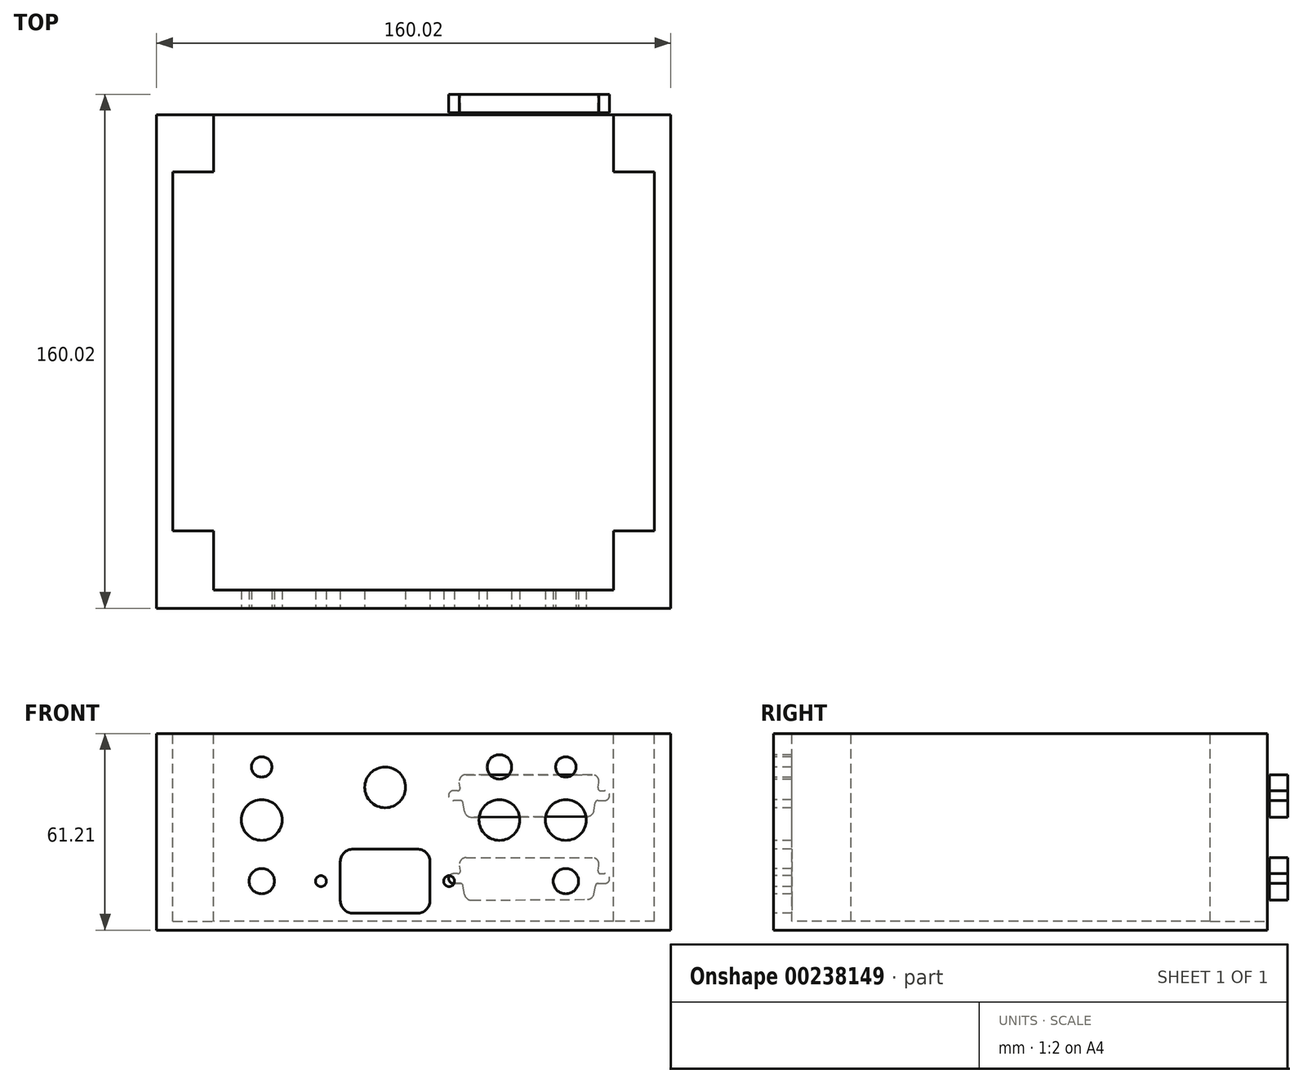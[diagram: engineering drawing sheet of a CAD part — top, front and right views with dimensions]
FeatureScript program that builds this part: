
annotation { "Feature Type Name" : "Feature", "Feature Type Description" : "" }
export const myFeature = defineFeature(function(context is Context, id is Id, definition is map)
    precondition{}
    {
        {
            var Q0;
            Q0=qCreatedBy(makeId("Top.planeOp"),FACE);
            var sketch = newSketch(context, id + "F0", { "sketchPlane" : qUnion([Q0])});
            skLineSegment(sketch, "E0.bottom", {"start": v(0, 0) * mm, "end": v(160.02, 0) * mm});
            skLineSegment(sketch, "E0.top", {"start": v(0, 160.02) * mm, "end": v(160.02, 160.02) * mm});
            skLineSegment(sketch, "E0.left", {"start": v(0, 0) * mm, "end": v(0, 160.02) * mm});
            skLineSegment(sketch, "E0.right", {"start": v(160.02, 0) * mm, "end": v(160.02, 160.02) * mm});
            skSolve(sketch);
        }
        {
            var Q0;
            Q0=makeQuery(id+"F0.imprint","IMPRINT",FACE,{"disambiguationData":[TD([[makeQuery(id+"F0.imprint","IMPRINT",EDGE,{"derivedFrom":sQuery(id+"F0.wireOp",EDGE,"E0.bottom")}),1.0]])]});
            extrude(context, id + "F1", {"entities" : qUnion([Q0]), "oppositeDirection" : true, "depth" : 61.2 * mm});
        }
        {
            var Q0;
            Q0=makeQuery(id+"F1.opExtrude","CAP_FACE",FACE,{"disambiguationData":[OSD([sQuery(id+"F0.wireOp",EDGE,"E0.bottom"),sQuery(id+"F0.wireOp",EDGE,"E0.top"),sQuery(id+"F0.wireOp",EDGE,"E0.left"),sQuery(id+"F0.wireOp",EDGE,"E0.right")])],"isStart":true});
            var sketch = newSketch(context, id + "F2", { "sketchPlane" : qUnion([Q0])});
            skLineSegment(sketch, "E1.bottom", {"start": v(5.08, 154.3) * mm, "end": v(154.94, 154.3) * mm});
            skLineSegment(sketch, "E1.top", {"start": v(5.08, 5.71) * mm, "end": v(154.94, 5.72) * mm});
            skLineSegment(sketch, "E1.left", {"start": v(5.08, 154.3) * mm, "end": v(5.08, 5.71) * mm});
            skLineSegment(sketch, "E1.right", {"start": v(154.94, 154.3) * mm, "end": v(154.94, 5.72) * mm});
            skLineSegment(sketch, "E2", {"start": v(5.08, 24.13) * mm, "end": v(17.78, 24.13) * mm});
            skLineSegment(sketch, "E3", {"start": v(17.78, 24.13) * mm, "end": v(17.78, 5.71) * mm});
            skLineSegment(sketch, "E4", {"start": v(154.94, 24.13) * mm, "end": v(142.24, 24.13) * mm});
            skLineSegment(sketch, "E5", {"start": v(142.24, 24.13) * mm, "end": v(142.24, 5.72) * mm});
            skLineSegment(sketch, "E6", {"start": v(5.08, 135.9) * mm, "end": v(17.78, 135.9) * mm});
            skLineSegment(sketch, "E7", {"start": v(17.78, 135.9) * mm, "end": v(17.78, 154.3) * mm});
            skLineSegment(sketch, "E8", {"start": v(154.94, 135.9) * mm, "end": v(142.24, 135.9) * mm});
            skLineSegment(sketch, "E9", {"start": v(142.24, 135.9) * mm, "end": v(142.24, 154.3) * mm});
            skSolve(sketch);
        }
        {
            var Q0;
            {var subQ3=sQuery(id+"F2.wireOp",EDGE,"E2");Q0=makeQuery(id+"F2.imprint","IMPRINT",FACE,{"disambiguationData":[TD([[makeQuery(id+"F2.imprint","IMPRINT",EDGE,{"derivedFrom":subQ3}),1.0]])]});}
            extrude(context, id + "F3", {"entities" : qUnion([Q0]), "operationType" : NewBodyOperationType.REMOVE, "oppositeDirection" : true, "depth" : 58.42 * mm});
        }
        {
            var Q0;
            Q0=makeQuery(id+"F1.opExtrude","SWEPT_FACE",FACE,{"disambiguationData":[OSD([sQuery(id+"F0.wireOp",EDGE,"E0.bottom")])]});
            var sketch = newSketch(context, id + "F4", { "sketchPlane" : qUnion([Q0])});
            skCircle(sketch, "E10", {"center": v(32.7, -45.97) * mm, "radius": 3.94 * mm});
            skCircle(sketch, "E11.1.0.0", {"center": v(127.34, -45.97) * mm, "radius": 3.94 * mm});
            skLineSegment(sketch, "E11.direction1", {"start": v(32.7, -45.97) * mm, "end": v(127.34, -45.97) * mm, "construction": true});
            skSolve(sketch);
        }
        {
            var Q0;
            Q0=makeQuery(id+"F4.imprint","IMPRINT",FACE,{"disambiguationData":[TD([[makeQuery(id+"F4.imprint","IMPRINT",EDGE,{"derivedFrom":sQuery(id+"F4.wireOp",EDGE,"E10")}),1.0]])]});
            var Q1;
            Q1=makeQuery(id+"F4.imprint","IMPRINT",FACE,{"disambiguationData":[TD([[makeQuery(id+"F4.imprint","IMPRINT",EDGE,{"derivedFrom":sQuery(id+"F4.wireOp",EDGE,"E11.1.0.0")}),1.0]])]});
            extrude(context, id + "F5", {"entities" : qUnion([Q0, Q1]), "operationType" : NewBodyOperationType.REMOVE, "oppositeDirection" : true, "depth" : 6.35 * mm});
        }
        {
            var Q0;
            Q0=makeQuery(id+"F1.opExtrude","SWEPT_FACE",FACE,{"disambiguationData":[OSD([sQuery(id+"F0.wireOp",EDGE,"E0.bottom")])]});
            var sketch = newSketch(context, id + "F6", { "sketchPlane" : qUnion([Q0])});
            skLineSegment(sketch, "E12.bottom", {"start": v(61.14, -35.98) * mm, "end": v(81.1, -35.98) * mm});
            skLineSegment(sketch, "E12.top", {"start": v(61.14, -55.97) * mm, "end": v(81.1, -55.97) * mm});
            skLineSegment(sketch, "E12.left", {"start": v(57.15, -39.97) * mm, "end": v(57.15, -51.98) * mm});
            skLineSegment(sketch, "E12.right", {"start": v(85.1, -39.97) * mm, "end": v(85.1, -51.98) * mm});
            skPoint(sketch, "E13.visualSharp", {"position": v(57.15, -35.98) * mm});
            skArc(sketch, "E13.filletArc", {"start": v(61.14, -35.98) * mm, "mid": v(58.32, -37.15) * mm, "end": v(57.15, -39.97) * mm});
            skPoint(sketch, "E14.visualSharp", {"position": v(57.15, -55.97) * mm});
            skArc(sketch, "E14.filletArc", {"start": v(57.15, -51.98) * mm, "mid": v(58.32, -54.8) * mm, "end": v(61.14, -55.97) * mm});
            skPoint(sketch, "E15.visualSharp", {"position": v(85.1, -55.97) * mm});
            skArc(sketch, "E15.filletArc", {"start": v(81.1, -55.97) * mm, "mid": v(83.92, -54.8) * mm, "end": v(85.1, -51.98) * mm});
            skPoint(sketch, "E16.visualSharp", {"position": v(85.1, -35.98) * mm});
            skArc(sketch, "E16.filletArc", {"start": v(85.1, -39.97) * mm, "mid": v(83.92, -37.15) * mm, "end": v(81.1, -35.98) * mm});
            skSolve(sketch);
        }
        {
            var Q0;
            Q0=makeQuery(id+"F6.imprint","IMPRINT",FACE,{"disambiguationData":[TD([[makeQuery(id+"F6.imprint","IMPRINT",EDGE,{"derivedFrom":sQuery(id+"F6.wireOp",EDGE,"E12.bottom")}),-1.0]])]});
            extrude(context, id + "F7", {"entities" : qUnion([Q0]), "operationType" : NewBodyOperationType.REMOVE, "oppositeDirection" : true, "depth" : 6.35 * mm});
        }
        {
            var Q0;
            Q0=makeQuery(id+"F1.opExtrude","SWEPT_FACE",FACE,{"disambiguationData":[OSD([sQuery(id+"F0.wireOp",EDGE,"E0.bottom")])]});
            var sketch = newSketch(context, id + "F8", { "sketchPlane" : qUnion([Q0])});
            skCircle(sketch, "E17", {"center": v(51.13, -45.97) * mm, "radius": 1.7 * mm});
            skCircle(sketch, "E18.1.0.0", {"center": v(91, -45.97) * mm, "radius": 1.7 * mm});
            skLineSegment(sketch, "E18.direction1", {"start": v(51.13, -45.97) * mm, "end": v(91, -45.97) * mm, "construction": true});
            skSolve(sketch);
        }
        {
            var Q0;
            Q0=makeQuery(id+"F8.imprint","IMPRINT",FACE,{"disambiguationData":[TD([[makeQuery(id+"F8.imprint","IMPRINT",EDGE,{"derivedFrom":sQuery(id+"F8.wireOp",EDGE,"E17")}),1.0]])]});
            var Q1;
            Q1=makeQuery(id+"F8.imprint","IMPRINT",FACE,{"disambiguationData":[TD([[makeQuery(id+"F8.imprint","IMPRINT",EDGE,{"derivedFrom":sQuery(id+"F8.wireOp",EDGE,"E18.1.0.0")}),1.0]])]});
            extrude(context, id + "F9", {"entities" : qUnion([Q0, Q1]), "operationType" : NewBodyOperationType.REMOVE, "oppositeDirection" : true, "depth" : 6.35 * mm});
        }
        {
            var Q0;
            Q0=makeQuery(id+"F1.opExtrude","SWEPT_FACE",FACE,{"disambiguationData":[OSD([sQuery(id+"F0.wireOp",EDGE,"E0.bottom")])]});
            var sketch = newSketch(context, id + "F10", { "sketchPlane" : qUnion([Q0])});
            skLineSegment(sketch, "E19.bottom", {"start": v(46.35, -34.98) * mm, "end": v(95.88, -34.98) * mm});
            skLineSegment(sketch, "E19.top", {"start": v(46.35, -56.97) * mm, "end": v(95.88, -56.97) * mm});
            skLineSegment(sketch, "E19.left", {"start": v(46.35, -34.98) * mm, "end": v(46.35, -56.97) * mm});
            skLineSegment(sketch, "E19.right", {"start": v(95.88, -34.98) * mm, "end": v(95.88, -56.97) * mm});
            skSolve(sketch);
        }
        {
            var Q0;
            Q0=makeQuery(id+"F10.imprint","IMPRINT",FACE,{"disambiguationData":[TD([[makeQuery(id+"F10.imprint","IMPRINT",EDGE,{"derivedFrom":sQuery(id+"F10.wireOp",EDGE,"E19.bottom")}),1.0]])]});
            var sketch = newSketch(context, id + "F11", { "sketchPlane" : qUnion([Q0])});
            skCircle(sketch, "E20", {"center": v(32.69, -26.92) * mm, "radius": 6.35 * mm});
            skCircle(sketch, "E21.1.0.0", {"center": v(127.33, -26.92) * mm, "radius": 6.35 * mm});
            skLineSegment(sketch, "E21.direction1", {"start": v(32.69, -26.92) * mm, "end": v(127.33, -26.92) * mm, "construction": true});
            skSolve(sketch);
        }
        {
            var Q0;
            Q0=makeQuery(id+"F11.imprint","IMPRINT",FACE,{"disambiguationData":[TD([[makeQuery(id+"F11.imprint","IMPRINT",EDGE,{"derivedFrom":sQuery(id+"F11.wireOp",EDGE,"E20")}),1.0]])]});
            var Q1;
            Q1=makeQuery(id+"F11.imprint","IMPRINT",FACE,{"disambiguationData":[TD([[makeQuery(id+"F11.imprint","IMPRINT",EDGE,{"derivedFrom":sQuery(id+"F11.wireOp",EDGE,"E21.1.0.0")}),1.0]])]});
            extrude(context, id + "F12", {"entities" : qUnion([Q0, Q1]), "operationType" : NewBodyOperationType.REMOVE, "oppositeDirection" : true, "depth" : 6.35 * mm});
        }
        {
            var Q0;
            Q0=makeQuery(id+"F10.imprint","IMPRINT",FACE,{"disambiguationData":[TD([[makeQuery(id+"F10.imprint","IMPRINT",EDGE,{"derivedFrom":sQuery(id+"F10.wireOp",EDGE,"E19.bottom")}),1.0]])]});
            var sketch = newSketch(context, id + "F13", { "sketchPlane" : qUnion([Q0])});
            skCircle(sketch, "E22", {"center": v(32.69, -10.41) * mm, "radius": 3.18 * mm});
            skCircle(sketch, "E23.1.0.0", {"center": v(127.33, -10.41) * mm, "radius": 3.18 * mm});
            skLineSegment(sketch, "E23.direction1", {"start": v(32.69, -10.41) * mm, "end": v(127.33, -10.41) * mm, "construction": true});
            skSolve(sketch);
        }
        {
            var Q0;
            Q0 = qSketchRegion(id + "F13", true);
            extrude(context, id + "F14", {"entities" : qUnion([Q0]), "operationType" : NewBodyOperationType.REMOVE, "oppositeDirection" : true, "depth" : 6.35 * mm});
        }
        {
            var Q0;
            Q0=makeQuery(id+"F10.imprint","IMPRINT",FACE,{"disambiguationData":[TD([[makeQuery(id+"F10.imprint","IMPRINT",EDGE,{"derivedFrom":sQuery(id+"F10.wireOp",EDGE,"E19.bottom")}),1.0]])]});
            var sketch = newSketch(context, id + "F15", { "sketchPlane" : qUnion([Q0])});
            skCircle(sketch, "E24", {"center": v(71.12, -16.76) * mm, "radius": 6.35 * mm});
            skSolve(sketch);
        }
        {
            var Q0;
            Q0=makeQuery(id+"F15.imprint","IMPRINT",FACE,{"disambiguationData":[TD([[makeQuery(id+"F15.imprint","IMPRINT",EDGE,{"derivedFrom":sQuery(id+"F15.wireOp",EDGE,"E24")}),1.0]])]});
            extrude(context, id + "F16", {"entities" : qUnion([Q0]), "operationType" : NewBodyOperationType.REMOVE, "oppositeDirection" : true, "depth" : 6.35 * mm});
        }
        {
            var Q0;
            Q0=makeQuery(id+"F10.imprint","IMPRINT",FACE,{"disambiguationData":[TD([[makeQuery(id+"F10.imprint","IMPRINT",EDGE,{"derivedFrom":sQuery(id+"F10.wireOp",EDGE,"E19.bottom")}),1.0]])]});
            var sketch = newSketch(context, id + "F17", { "sketchPlane" : qUnion([Q0])});
            skCircle(sketch, "E25", {"center": v(106.68, -26.92) * mm, "radius": 6.35 * mm});
            skSolve(sketch);
        }
        {
            var Q0;
            Q0 = qSketchRegion(id + "F17", true);
            extrude(context, id + "F18", {"entities" : qUnion([Q0]), "operationType" : NewBodyOperationType.REMOVE, "oppositeDirection" : true, "depth" : 6.35 * mm});
        }
        {
            var Q0;
            Q0=makeQuery(id+"F10.imprint","IMPRINT",FACE,{"disambiguationData":[TD([[makeQuery(id+"F10.imprint","IMPRINT",EDGE,{"derivedFrom":sQuery(id+"F10.wireOp",EDGE,"E19.bottom")}),1.0]])]});
            var sketch = newSketch(context, id + "F19", { "sketchPlane" : qUnion([Q0])});
            skCircle(sketch, "E26", {"center": v(106.68, -10.41) * mm, "radius": 3.81 * mm});
            skSolve(sketch);
        }
        {
            var Q0;
            Q0 = qSketchRegion(id + "F19", true);
            extrude(context, id + "F20", {"entities" : qUnion([Q0]), "operationType" : NewBodyOperationType.REMOVE, "oppositeDirection" : true, "depth" : 6.35 * mm});
        }
        {
            var Q0;
            Q0=makeQuery(id+"F1.opExtrude","SWEPT_FACE",FACE,{"disambiguationData":[OSD([sQuery(id+"F0.wireOp",EDGE,"E0.top")])]});
            var sketch = newSketch(context, id + "F21", { "sketchPlane" : qUnion([Q0])});
            skSolve(sketch);
        }
        {
            var Q0;
            {var subQ0=sQuery(id+"F0.wireOp",EDGE,"E0.top");Q0=makeQuery(id+"F21.imprint","IMPRINT",FACE,{"disambiguationData":[TD([[makeQuery(id+"F21.imprint","IMPRINT",EDGE,{"derivedFrom":makeQuery(id+"F1.opExtrude","CAP_EDGE",EDGE,{"disambiguationData":[OSD([subQ0])],"isStart":true})}),1.0]])]});}
            var sketch = newSketch(context, id + "F22", { "sketchPlane" : qUnion([Q0])});
            skLineSegment(sketch, "E27", {"start": v(-140.97, -45.17) * mm, "end": v(-139.45, -45.17) * mm, "construction": true});
            skArc(sketch, "E28", {"start": v(-139.45, -46.7) * mm, "mid": v(-140.97, -45.17) * mm, "end": v(-139.45, -43.65) * mm});
            skLineSegment(sketch, "E29", {"start": v(-90.88, -45.17) * mm, "end": v(-92.4, -45.17) * mm, "construction": true});
            skArc(sketch, "E30", {"start": v(-92.4, -43.65) * mm, "mid": v(-90.88, -45.17) * mm, "end": v(-92.4, -46.7) * mm});
            skLineSegment(sketch, "E31", {"start": v(-135.56, -38.66) * mm, "end": v(-96.31, -38.66) * mm});
            skLineSegment(sketch, "E32", {"start": v(-137.64, -41.13) * mm, "end": v(-137.36, -42.7) * mm});
            skLineSegment(sketch, "E33", {"start": v(-94.24, -41.13) * mm, "end": v(-94.51, -42.7) * mm});
            skLineSegment(sketch, "E34", {"start": v(-134.03, -51.66) * mm, "end": v(-97.92, -51.9) * mm});
            skLineSegment(sketch, "E35", {"start": v(-92.4, -43.65) * mm, "end": v(-93.71, -43.65) * mm});
            skLineSegment(sketch, "E36", {"start": v(-92.4, -46.7) * mm, "end": v(-94.54, -46.7) * mm});
            skLineSegment(sketch, "E37", {"start": v(-139.45, -43.65) * mm, "end": v(-138.16, -43.65) * mm});
            skLineSegment(sketch, "E38", {"start": v(-139.45, -46.7) * mm, "end": v(-137.34, -46.7) * mm});
            skLineSegment(sketch, "E39.trimOffspring", {"start": v(-136.54, -47.37) * mm, "end": v(-136.09, -49.92) * mm});
            skLineSegment(sketch, "E40.trimOffspring", {"start": v(-95.34, -47.37) * mm, "end": v(-95.83, -50.15) * mm});
            skPoint(sketch, "E41.visualSharp", {"position": v(-135.78, -51.65) * mm});
            skArc(sketch, "E41.filletArc", {"start": v(-136.09, -49.92) * mm, "mid": v(-135.37, -51.17) * mm, "end": v(-134.03, -51.66) * mm});
            skPoint(sketch, "E42.visualSharp", {"position": v(-96.14, -51.9) * mm});
            skArc(sketch, "E42.filletArc", {"start": v(-97.92, -51.9) * mm, "mid": v(-96.55, -51.4) * mm, "end": v(-95.83, -50.15) * mm});
            skPoint(sketch, "E43.visualSharp", {"position": v(-93.8, -38.66) * mm});
            skArc(sketch, "E43.filletArc", {"start": v(-94.24, -41.13) * mm, "mid": v(-94.7, -39.41) * mm, "end": v(-96.31, -38.66) * mm});
            skPoint(sketch, "E44.visualSharp", {"position": v(-138.07, -38.66) * mm});
            skArc(sketch, "E44.filletArc", {"start": v(-135.56, -38.66) * mm, "mid": v(-137.18, -39.41) * mm, "end": v(-137.64, -41.13) * mm});
            skPoint(sketch, "E45.visualSharp", {"position": v(-136.66, -46.7) * mm});
            skArc(sketch, "E45.filletArc", {"start": v(-136.54, -47.37) * mm, "mid": v(-136.82, -46.89) * mm, "end": v(-137.34, -46.7) * mm});
            skPoint(sketch, "E46.visualSharp", {"position": v(-137.2, -43.65) * mm});
            skArc(sketch, "E46.filletArc", {"start": v(-138.16, -43.65) * mm, "mid": v(-137.54, -43.36) * mm, "end": v(-137.36, -42.7) * mm});
            skPoint(sketch, "E47.visualSharp", {"position": v(-94.68, -43.65) * mm});
            skArc(sketch, "E47.filletArc", {"start": v(-94.51, -42.7) * mm, "mid": v(-94.34, -43.36) * mm, "end": v(-93.71, -43.65) * mm});
            skPoint(sketch, "E48.visualSharp", {"position": v(-95.22, -46.7) * mm});
            skArc(sketch, "E48.filletArc", {"start": v(-94.54, -46.7) * mm, "mid": v(-95.06, -46.89) * mm, "end": v(-95.34, -47.37) * mm});
            skLineSegment(sketch, "E49", {"start": v(-140.94, -19.32) * mm, "end": v(-139.42, -19.32) * mm, "construction": true});
            skArc(sketch, "E50", {"start": v(-139.42, -20.85) * mm, "mid": v(-140.94, -19.32) * mm, "end": v(-139.42, -17.8) * mm});
            skLineSegment(sketch, "E51", {"start": v(-90.85, -19.32) * mm, "end": v(-92.38, -19.32) * mm, "construction": true});
            skArc(sketch, "E52", {"start": v(-92.38, -17.8) * mm, "mid": v(-90.85, -19.32) * mm, "end": v(-92.38, -20.85) * mm});
            skLineSegment(sketch, "E53", {"start": v(-135.54, -12.8) * mm, "end": v(-96.29, -12.8) * mm});
            skLineSegment(sketch, "E54", {"start": v(-137.61, -15.28) * mm, "end": v(-137.34, -16.85) * mm});
            skLineSegment(sketch, "E55", {"start": v(-94.21, -15.28) * mm, "end": v(-94.49, -16.85) * mm});
            skLineSegment(sketch, "E56", {"start": v(-134, -25.82) * mm, "end": v(-97.9, -26.04) * mm});
            skLineSegment(sketch, "E57", {"start": v(-92.38, -17.8) * mm, "end": v(-93.69, -17.8) * mm});
            skLineSegment(sketch, "E58", {"start": v(-92.38, -20.85) * mm, "end": v(-94.51, -20.85) * mm});
            skLineSegment(sketch, "E59", {"start": v(-139.42, -17.8) * mm, "end": v(-138.14, -17.8) * mm});
            skLineSegment(sketch, "E60", {"start": v(-139.42, -20.85) * mm, "end": v(-137.31, -20.85) * mm});
            skLineSegment(sketch, "E61.trimOffspring", {"start": v(-136.51, -21.52) * mm, "end": v(-136.06, -24.07) * mm});
            skLineSegment(sketch, "E62.trimOffspring", {"start": v(-95.31, -21.52) * mm, "end": v(-95.8, -24.3) * mm});
            skPoint(sketch, "E63.visualSharp", {"position": v(-135.76, -25.8) * mm});
            skArc(sketch, "E63.filletArc", {"start": v(-136.06, -24.07) * mm, "mid": v(-135.35, -25.32) * mm, "end": v(-134, -25.82) * mm});
            skPoint(sketch, "E64.visualSharp", {"position": v(-96.11, -26.05) * mm});
            skArc(sketch, "E64.filletArc", {"start": v(-97.9, -26.04) * mm, "mid": v(-96.53, -25.55) * mm, "end": v(-95.8, -24.3) * mm});
            skPoint(sketch, "E65.visualSharp", {"position": v(-93.78, -12.8) * mm});
            skArc(sketch, "E65.filletArc", {"start": v(-94.21, -15.28) * mm, "mid": v(-94.67, -13.56) * mm, "end": v(-96.29, -12.8) * mm});
            skPoint(sketch, "E66.visualSharp", {"position": v(-138.05, -12.8) * mm});
            skArc(sketch, "E66.filletArc", {"start": v(-135.54, -12.8) * mm, "mid": v(-137.15, -13.56) * mm, "end": v(-137.61, -15.28) * mm});
            skPoint(sketch, "E67.visualSharp", {"position": v(-136.63, -20.85) * mm});
            skArc(sketch, "E67.filletArc", {"start": v(-136.51, -21.52) * mm, "mid": v(-136.79, -21.04) * mm, "end": v(-137.31, -20.85) * mm});
            skPoint(sketch, "E68.visualSharp", {"position": v(-137.17, -17.8) * mm});
            skArc(sketch, "E68.filletArc", {"start": v(-138.14, -17.8) * mm, "mid": v(-137.51, -17.51) * mm, "end": v(-137.34, -16.85) * mm});
            skPoint(sketch, "E69.visualSharp", {"position": v(-94.66, -17.8) * mm});
            skArc(sketch, "E69.filletArc", {"start": v(-94.49, -16.85) * mm, "mid": v(-94.3, -17.51) * mm, "end": v(-93.69, -17.8) * mm});
            skPoint(sketch, "E70.visualSharp", {"position": v(-95.2, -20.85) * mm});
            skArc(sketch, "E70.filletArc", {"start": v(-94.51, -20.85) * mm, "mid": v(-95.03, -21.04) * mm, "end": v(-95.31, -21.52) * mm});
            skSolve(sketch);
        }
        {
            var Q0;
            Q0=makeQuery(id+"F22.imprint","IMPRINT",FACE,{"disambiguationData":[TD([[makeQuery(id+"F22.imprint","IMPRINT",EDGE,{"derivedFrom":sQuery(id+"F22.wireOp",EDGE,"E50")}),-1.0]])]});
            var Q1;
            Q1=makeQuery(id+"F22.imprint","IMPRINT",FACE,{"disambiguationData":[TD([[makeQuery(id+"F22.imprint","IMPRINT",EDGE,{"derivedFrom":sQuery(id+"F22.wireOp",EDGE,"E28")}),-1.0]])]});
            extrude(context, id + "F23", {"entities" : qUnion([Q0, Q1]), "operationType" : NewBodyOperationType.REMOVE, "oppositeDirection" : true, "depth" : 6.35 * mm});
        }
        {
            var Q0;
            {var subQ0=sQuery(id+"F0.wireOp",EDGE,"E0.top");Q0=makeQuery(id+"F21.imprint","IMPRINT",FACE,{"disambiguationData":[TD([[makeQuery(id+"F21.imprint","IMPRINT",EDGE,{"derivedFrom":makeQuery(id+"F1.opExtrude","CAP_EDGE",EDGE,{"disambiguationData":[OSD([subQ0])],"isStart":true})}),1.0]])]});}
            var sketch = newSketch(context, id + "F24", { "sketchPlane" : qUnion([Q0])});
            skLineSegment(sketch, "E71.bottom", {"start": v(-52.07, -38.99) * mm, "end": v(-39.37, -38.99) * mm});
            skLineSegment(sketch, "E71.top", {"start": v(-52.07, -51.69) * mm, "end": v(-39.37, -51.69) * mm});
            skLineSegment(sketch, "E71.left", {"start": v(-52.07, -38.99) * mm, "end": v(-52.07, -51.69) * mm});
            skLineSegment(sketch, "E71.right", {"start": v(-39.37, -38.99) * mm, "end": v(-39.37, -51.69) * mm});
            skCircle(sketch, "E72", {"center": v(-60.7, -45.34) * mm, "radius": 1.83 * mm});
            skCircle(sketch, "E73.1.0.0", {"center": v(-30.7, -45.34) * mm, "radius": 1.83 * mm});
            skLineSegment(sketch, "E73.direction1", {"start": v(-60.7, -45.34) * mm, "end": v(-30.7, -45.34) * mm, "construction": true});
            skSolve(sketch);
        }
        {
            var Q0;
            Q0=makeQuery(id+"F24.imprint","IMPRINT",FACE,{"disambiguationData":[TD([[makeQuery(id+"F24.imprint","IMPRINT",EDGE,{"derivedFrom":sQuery(id+"F24.wireOp",EDGE,"E71.bottom")}),-1.0]])]});
            var Q1;
            Q1=makeQuery(id+"F24.imprint","IMPRINT",FACE,{"disambiguationData":[TD([[makeQuery(id+"F24.imprint","IMPRINT",EDGE,{"derivedFrom":sQuery(id+"F24.wireOp",EDGE,"E72")}),1.0]])]});
            var Q2;
            Q2=makeQuery(id+"F24.imprint","IMPRINT",FACE,{"disambiguationData":[TD([[makeQuery(id+"F24.imprint","IMPRINT",EDGE,{"derivedFrom":sQuery(id+"F24.wireOp",EDGE,"E73.1.0.0")}),1.0]])]});
            extrude(context, id + "F25", {"entities" : qUnion([Q0, Q1, Q2]), "operationType" : NewBodyOperationType.REMOVE, "oppositeDirection" : true, "depth" : 6.35 * mm});
        }
    });
